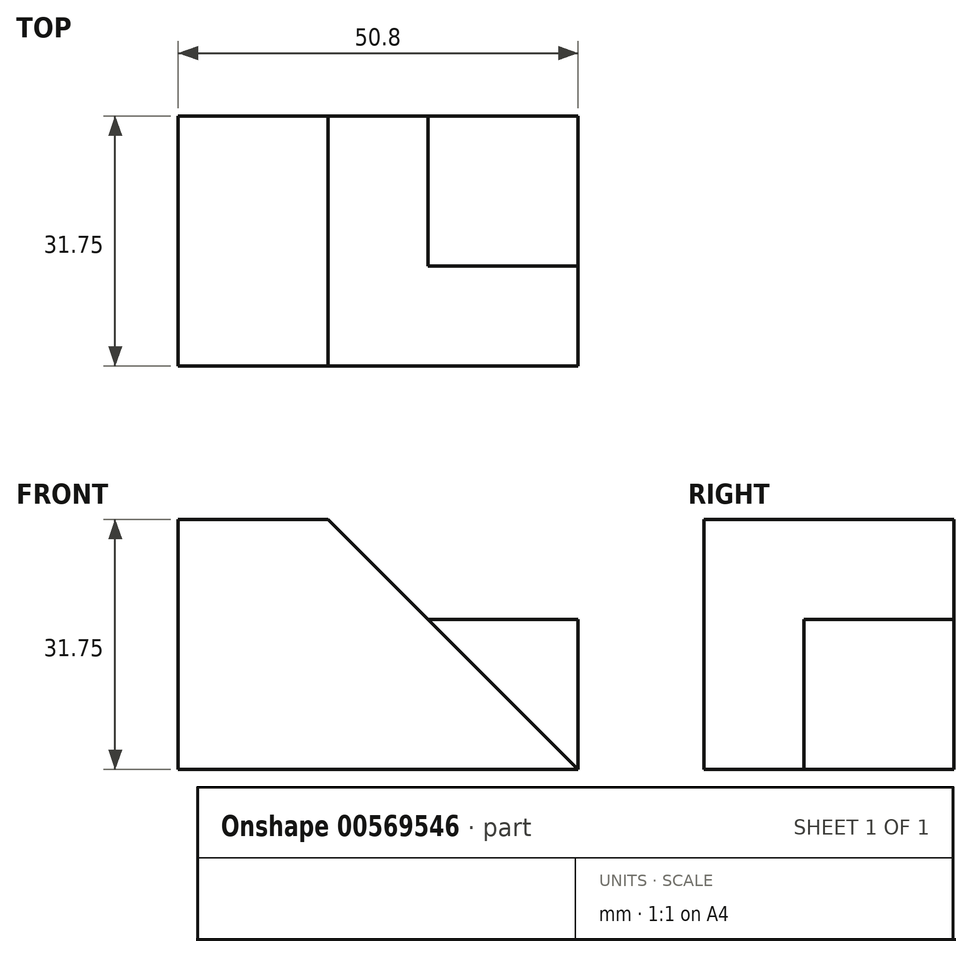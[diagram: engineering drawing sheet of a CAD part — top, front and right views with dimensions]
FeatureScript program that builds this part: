
annotation { "Feature Type Name" : "Feature", "Feature Type Description" : "" }
export const myFeature = defineFeature(function(context is Context, id is Id, definition is map)
    precondition{}
    {
        {
            var Q0;
            Q0=qCreatedBy(makeId("Front.planeOp"),FACE);
            var sketch = newSketch(context, id + "F0", { "sketchPlane" : qUnion([Q0])});
            skLineSegment(sketch, "E0", {"start": v(-63.14, 51.65) * mm, "end": v(-63.14, 19.9) * mm});
            skLineSegment(sketch, "E1", {"start": v(-63.14, 19.9) * mm, "end": v(-12.34, 19.9) * mm});
            skLineSegment(sketch, "E2", {"start": v(-12.34, 19.9) * mm, "end": v(-12.34, 51.65) * mm});
            skLineSegment(sketch, "E3", {"start": v(-12.34, 51.65) * mm, "end": v(-63.14, 51.65) * mm});
            skSolve(sketch);
        }
        {
            var Q0;
            Q0 = qSketchRegion(id + "F0", true);
            extrude(context, id + "F1", {"entities" : qUnion([Q0]), "depth" : 31.75 * mm, "offsetDistance" : 25.4 * mm});
        }
        {
            var Q0;
            Q0=makeQuery(id+"F1.opExtrude","CAP_FACE",FACE,{"disambiguationData":[OSD([sQuery(id+"F0.wireOp",EDGE,"E0"),sQuery(id+"F0.wireOp",EDGE,"E1"),sQuery(id+"F0.wireOp",EDGE,"E2"),sQuery(id+"F0.wireOp",EDGE,"E3")])],"isStart":false});
            var sketch = newSketch(context, id + "F2", { "sketchPlane" : qUnion([Q0])});
            skLineSegment(sketch, "E4", {"start": v(-44.1, 51.65) * mm, "end": v(-12.34, 19.9) * mm});
            skLineSegment(sketch, "E5", {"start": v(-12.34, 19.9) * mm, "end": v(-12.34, 51.65) * mm});
            skLineSegment(sketch, "E6", {"start": v(-12.34, 51.65) * mm, "end": v(-44.1, 51.65) * mm});
            skSolve(sketch);
        }
        {
            var Q0;
            Q0 = qSketchRegion(id + "F2", true);
            extrude(context, id + "F3", {"entities" : qUnion([Q0]), "operationType" : NewBodyOperationType.REMOVE, "oppositeDirection" : true, "depth" : 12.7 * mm, "offsetDistance" : 25.4 * mm});
        }
        {
            var Q0;
            Q0=makeQuery(id+"F3.boolean.opBoolean","COPY",FACE,{"derivedFrom":makeQuery(id+"F3.opExtrude","CAP_FACE",FACE,{"disambiguationData":[OSD([sQuery(id+"F2.wireOp",EDGE,"E4"),sQuery(id+"F2.wireOp",EDGE,"E5"),sQuery(id+"F2.wireOp",EDGE,"E6")])],"isStart":false})});
            var sketch = newSketch(context, id + "F4", { "sketchPlane" : qUnion([Q0])});
            skLineSegment(sketch, "E7", {"start": v(-44.1, 51.65) * mm, "end": v(-31.4, 38.95) * mm});
            skLineSegment(sketch, "E8", {"start": v(-31.4, 38.95) * mm, "end": v(-12.34, 38.95) * mm});
            skLineSegment(sketch, "E9", {"start": v(-12.34, 38.95) * mm, "end": v(-12.34, 51.65) * mm});
            skLineSegment(sketch, "E10", {"start": v(-12.34, 51.65) * mm, "end": v(-44.1, 51.65) * mm});
            skSolve(sketch);
        }
        {
            var Q0;
            Q0 = qSketchRegion(id + "F4", true);
            extrude(context, id + "F5", {"entities" : qUnion([Q0]), "operationType" : NewBodyOperationType.REMOVE, "oppositeDirection" : true, "depth" : 19.05 * mm, "offsetDistance" : 25.4 * mm});
        }
    });
